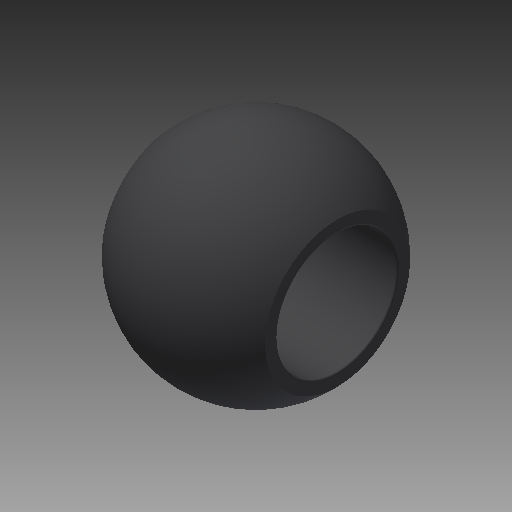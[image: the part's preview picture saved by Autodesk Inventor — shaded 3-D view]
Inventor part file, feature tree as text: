
AUTODESK INVENTOR PART (.ipt)
format: ipt  version: 2018 (Build 220112000, 112)  size: 151,040 bytes
history: native  units: mm
features: other x7, revolve x1, sketch x1
ambient origin geometry x8: Origin, YZ Plane, XZ Plane, XY Plane, X Axis, Y Axis, Z Axis, Center Point
bodies: Solid1 (feature_tree)
feature tree (9):
  revolve  "Revolution1"  [1 undecoded]
  other  "IP_1_BA_XY"
  other  "IP_1_BA_YZ"
  other  "IP_1_BA_ZX"
  other  "IP_1_BA_X"
  other  "IP_1_BA_Y"
  other  "IP_1_BA_Z"
  other  "IP_1_BA_Center"
  sketch  "Sketch_1"  dims[d0=360.0deg]
note: 1 required parameter value undecoded (feature->parameter linkage not recoverable at this tier; creation-order binding heuristic only, values carry confidence <= 0.55)
